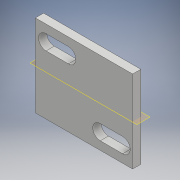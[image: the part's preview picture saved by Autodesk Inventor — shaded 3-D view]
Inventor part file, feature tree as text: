
AUTODESK INVENTOR PART (.ipt)
format: ipt  version: 2017 (Build 210142000, 142)  size: 114,176 bytes
history: native  units: mm
features: extrude x1, plane x1, sketch x1
ambient origin geometry x8: Origin, YZ Plane, XZ Plane, XY Plane, X Axis, Y Axis, Z Axis, Center Point
bodies: Solid1 (feature_tree)
feature tree (3):
  extrude  "Extrusion1"  Depth=22.0mm
  plane  "Work Plane1"
  sketch  "Sketch1"  dims[d0=26.0mm d1=22.0mm d5=6.0mm d6=4.0mm d9=2.2mm d10=0.0mm d19=6.0mm d20=4.0mm d21=14.5mm]
